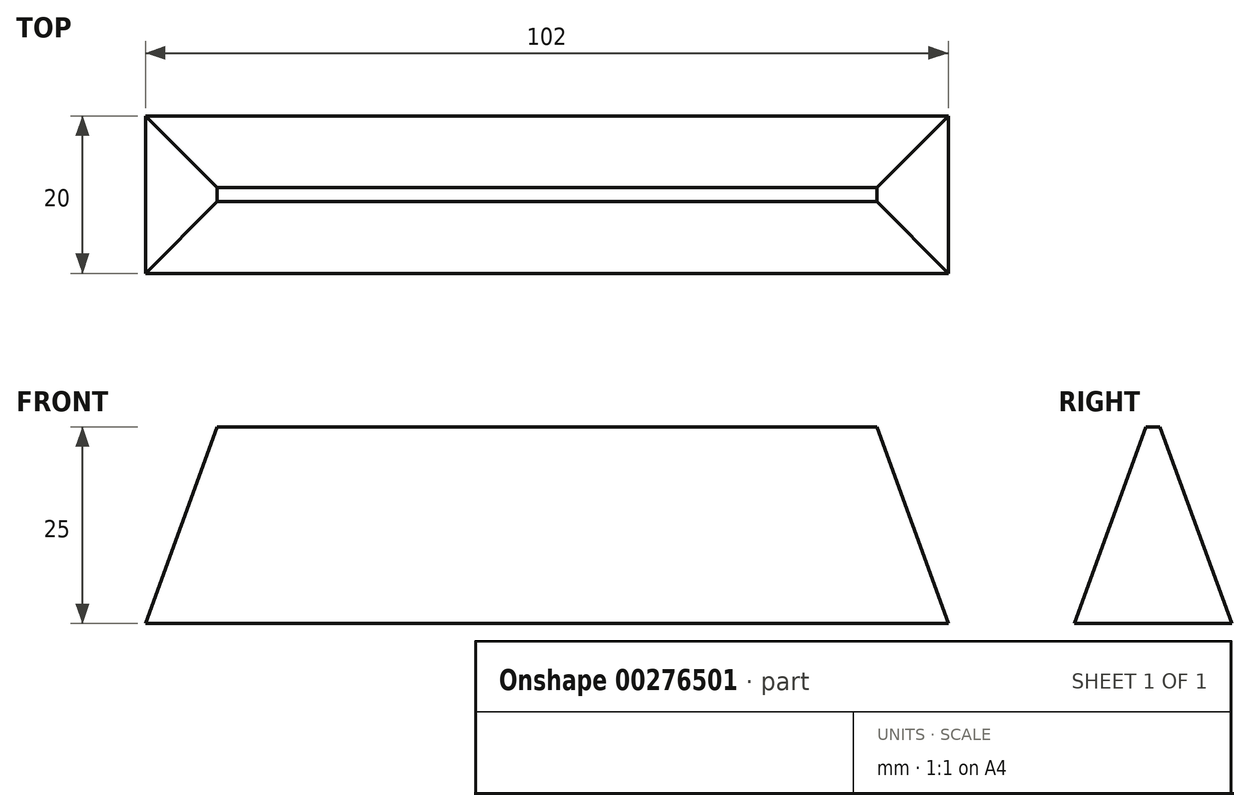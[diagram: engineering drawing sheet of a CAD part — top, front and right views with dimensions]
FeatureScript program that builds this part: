
annotation { "Feature Type Name" : "Feature", "Feature Type Description" : "" }
export const myFeature = defineFeature(function(context is Context, id is Id, definition is map)
    precondition{}
    {
        {
            var Q0;
            Q0=qCreatedBy(makeId("Top.planeOp"),FACE);
            var sketch = newSketch(context, id + "F0", { "sketchPlane" : qUnion([Q0])});
            skLineSegment(sketch, "E0.bottom", {"start": v(0, 0) * mm, "end": v(102, 0) * mm});
            skLineSegment(sketch, "E0.top", {"start": v(0, 20) * mm, "end": v(102, 20) * mm});
            skLineSegment(sketch, "E0.left", {"start": v(0, 0) * mm, "end": v(0, 20) * mm});
            skLineSegment(sketch, "E0.right", {"start": v(102, 0) * mm, "end": v(102, 20) * mm});
            skSolve(sketch);
        }
        {
            var Q0;
            Q0 = qSketchRegion(id + "F0", true);
            extrude(context, id + "F1", {"entities" : qUnion([Q0]), "depth" : 25 * mm, "hasDraft" : true, "draftAngle" : 20 * degree, "draftPullDirection" : true});
        }
    });
